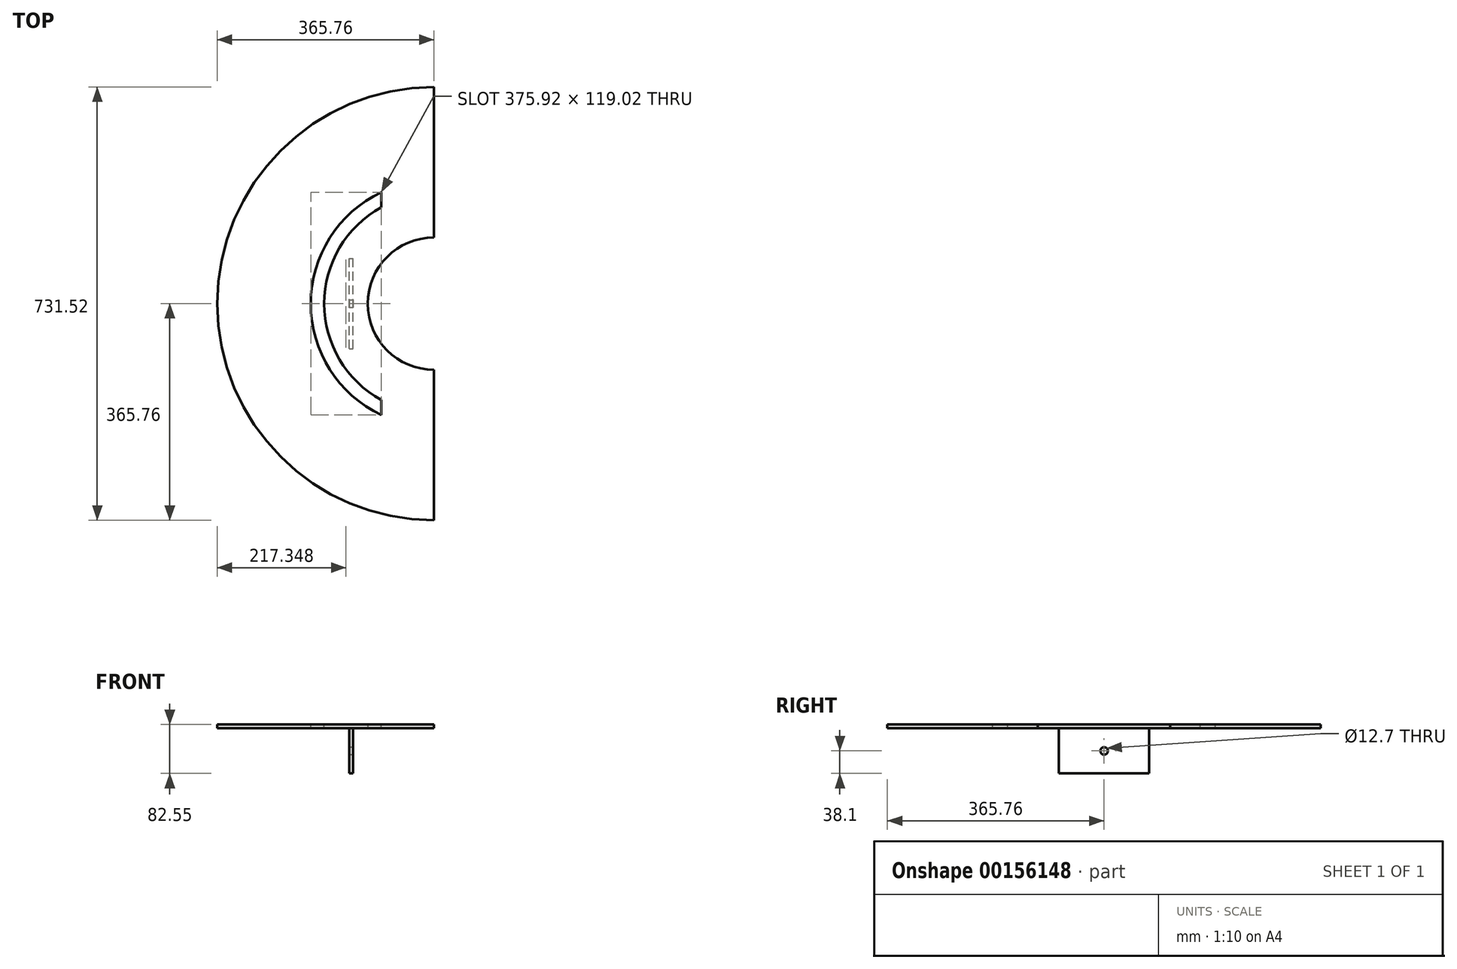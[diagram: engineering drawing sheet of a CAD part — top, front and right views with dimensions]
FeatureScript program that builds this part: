
annotation { "Feature Type Name" : "Feature", "Feature Type Description" : "" }
export const myFeature = defineFeature(function(context is Context, id is Id, definition is map)
    precondition{}
    {
        {
            var Q0;
            Q0=qCreatedBy(makeId("Top.planeOp"),FACE);
            var sketch = newSketch(context, id + "F0", { "sketchPlane" : qUnion([Q0])});
            skCircle(sketch, "E0", {"center": v(0, 0) * mm, "radius": 111.76 * mm});
            skCircle(sketch, "E1", {"center": v(0, 0) * mm, "radius": 365.76 * mm});
            skSolve(sketch);
        }
        {
            var Q0;
            Q0=makeQuery(id+"F0.imprint","IMPRINT",FACE,{"disambiguationData":[TD([[makeQuery(id+"F0.imprint","IMPRINT",EDGE,{"derivedFrom":sQuery(id+"F0.wireOp",EDGE,"E0")}),-1.0]])]});
            extrude(context, id + "F1", {"entities" : qUnion([Q0]), "depth" : 6.35 * mm});
        }
        {
            var Q0;
            Q0=makeQuery(id+"F1.opExtrude","CAP_FACE",FACE,{"disambiguationData":[OSD([sQuery(id+"F0.wireOp",EDGE,"E0"),sQuery(id+"F0.wireOp",EDGE,"E1")])],"isStart":false});
            var sketch = newSketch(context, id + "F2", { "sketchPlane" : qUnion([Q0])});
            skLineSegment(sketch, "E2.bottom", {"start": v(0, 394.93) * mm, "end": v(380.01, 394.93) * mm});
            skLineSegment(sketch, "E2.top", {"start": v(0, -392.69) * mm, "end": v(380.01, -392.69) * mm});
            skLineSegment(sketch, "E2.left", {"start": v(0, 394.93) * mm, "end": v(0, -392.69) * mm});
            skLineSegment(sketch, "E2.right", {"start": v(380.01, 394.93) * mm, "end": v(380.01, -392.69) * mm});
            skSolve(sketch);
        }
        {
            var Q0;
            Q0 = qSketchRegion(id + "F2", true);
            extrude(context, id + "F3", {"entities" : qUnion([Q0]), "operationType" : NewBodyOperationType.REMOVE, "endBound" : BoundingType.THROUGH_ALL, "oppositeDirection" : true, "depth" : 25.4 * mm});
        }
        {
            var Q0;
            Q0=makeQuery(id+"F1.opExtrude","CAP_FACE",FACE,{"disambiguationData":[OSD([sQuery(id+"F0.wireOp",EDGE,"E0"),sQuery(id+"F0.wireOp",EDGE,"E1")])],"isStart":false});
            var sketch = newSketch(context, id + "F4", { "sketchPlane" : qUnion([Q0])});
            skLineSegment(sketch, "E3.right", {"start": v(-88.9, -289.56) * mm, "end": v(-88.9, -264.16) * mm});
            skLineSegment(sketch, "E4.right", {"start": v(-88.9, 264.16) * mm, "end": v(-88.9, 289.56) * mm});
            skPoint(sketch, "E5.middle.positionSnap0", {"position": v(-365.76, 0) * mm});
            skPoint(sketch, "E5.centerSnap0", {"position": v(-365.76, 0) * mm});
            skLineSegment(sketch, "E6.left", {"start": v(-88.9, -162.56) * mm, "end": v(-88.9, -187.96) * mm});
            skLineSegment(sketch, "E7.left", {"start": v(-88.9, 187.96) * mm, "end": v(-88.9, 162.56) * mm});
            skCircle(sketch, "E8", {"center": v(0, 0) * mm, "radius": 302.9 * mm});
            skCircle(sketch, "E9", {"center": v(0, 0) * mm, "radius": 278.72 * mm});
            skCircle(sketch, "E10", {"center": v(0, 0) * mm, "radius": 207.92 * mm});
            skCircle(sketch, "E11", {"center": v(0, 0) * mm, "radius": 185.28 * mm});
            skLineSegment(sketch, "E12", {"start": v(-88.9, 289.56) * mm, "end": v(-88.9, 264.16) * mm});
            skLineSegment(sketch, "E13", {"start": v(-88.9, -264.16) * mm, "end": v(-88.9, -289.56) * mm});
            skSolve(sketch);
        }
        {
            var Q0;
            {var subQ0=sQuery(id+"F4.wireOp",EDGE,"E12");Q0=makeQuery(id+"F4.imprint","IMPRINT",FACE,{"disambiguationData":[TD([[makeQuery(id+"F4.imprint","IMPRINT",EDGE,{"derivedFrom":subQ0}),-1.0]])]});}
            var Q1;
            {var subQ0=sQuery(id+"F4.wireOp",EDGE,"E7.left");Q1=makeQuery(id+"F4.imprint","IMPRINT",FACE,{"disambiguationData":[TD([[makeQuery(id+"F4.imprint","IMPRINT",EDGE,{"derivedFrom":subQ0}),-1.0]])]});}
            extrude(context, id + "F5", {"entities" : qUnion([Q0, Q1]), "operationType" : NewBodyOperationType.REMOVE, "endBound" : BoundingType.THROUGH_ALL, "oppositeDirection" : true, "depth" : 25.4 * mm});
        }
        {
            var Q0;
            Q0=makeQuery(id+"F1.opExtrude","CAP_FACE",FACE,{"disambiguationData":[OSD([sQuery(id+"F0.wireOp",EDGE,"E0"),sQuery(id+"F0.wireOp",EDGE,"E1")])],"isStart":true});
            var sketch = newSketch(context, id + "F6", { "sketchPlane" : qUnion([Q0])});
            skLineSegment(sketch, "E14.bottom", {"start": v(-142.83, 76.2) * mm, "end": v(-136.48, 76.2) * mm});
            skLineSegment(sketch, "E14.top", {"start": v(-142.83, -76.2) * mm, "end": v(-136.48, -76.2) * mm});
            skLineSegment(sketch, "E14.left", {"start": v(-142.83, 76.2) * mm, "end": v(-142.83, -76.2) * mm});
            skLineSegment(sketch, "E14.right", {"start": v(-136.48, 76.2) * mm, "end": v(-136.48, -76.2) * mm});
            skSolve(sketch);
        }
        {
            var Q0;
            Q0 = qSketchRegion(id + "F6", true);
            extrude(context, id + "F7", {"entities" : qUnion([Q0]), "operationType" : NewBodyOperationType.ADD, "depth" : 76.2 * mm, "offsetDistance" : 25.4 * mm});
        }
        {
            var Q0;
            Q0=makeQuery(id+"F7.opExtrude","SWEPT_FACE",FACE,{"disambiguationData":[OSD([sQuery(id+"F6.wireOp",EDGE,"E14.right")])]});
            var sketch = newSketch(context, id + "F8", { "sketchPlane" : qUnion([Q0])});
            skCircle(sketch, "E15", {"center": v(0, -38.1) * mm, "radius": 6.35 * mm});
            skSolve(sketch);
        }
        {
            var Q0;
            Q0 = qSketchRegion(id + "F8", true);
            extrude(context, id + "F9", {"entities" : qUnion([Q0]), "operationType" : NewBodyOperationType.REMOVE, "endBound" : BoundingType.THROUGH_ALL, "oppositeDirection" : true, "depth" : 25.4 * mm, "offsetDistance" : 25.4 * mm});
        }
    });
